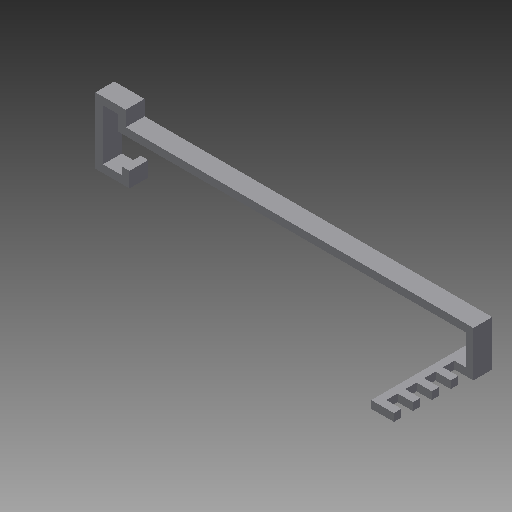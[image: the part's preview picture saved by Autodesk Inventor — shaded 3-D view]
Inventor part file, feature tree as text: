
AUTODESK INVENTOR PART (.ipt)
format: ipt  version: 2018.3 (Build 223284000, 284)  size: 239,616 bytes
history: native  units: mm
features: extrude x19, sketch x19
ambient origin geometry x8: Origin, YZ Plane, XZ Plane, XY Plane, X Axis, Y Axis, Z Axis, Center Point
bodies: Solid1 (feature_tree)
feature tree (38):
  extrude  "Extrusion1"  Depth=2.0mm
  extrude  "Extrusion2"  Depth=2.0mm TaperAngle=0.0deg
  extrude  "Extrusion3"  Depth=4.0mm TaperAngle=0.0deg
  extrude  "Extrusion5"  Depth=89.93mm TaperAngle=0.0deg
  extrude  "Extrusion6"  Depth=2.0mm
  extrude  "Extrusion7"  Depth=5.0mm TaperAngle=0.0deg
  extrude  "Extrusion8"  Depth=5.0mm TaperAngle=0.0deg
  extrude  "Extrusion9"  Depth=2.0mm
  extrude  "Extrusion10"  Depth=2.0mm
  extrude  "Extrusion11"  Depth=2.0mm
  extrude  "Extrusion12"  Depth=2.0mm
  extrude  "Extrusion13"  Depth=5.0mm TaperAngle=0.0deg
  extrude  "Extrusion14"  Depth=4.0mm TaperAngle=0.0deg
  extrude  "Extrusion15"  Depth=10.0mm TaperAngle=0.0deg
  extrude  "Extrusion16"  Depth=4.0mm TaperAngle=0.0deg
  extrude  "Extrusion17"  Depth=2.0mm
  extrude  "Extrusion18"  [1 undecoded]
  extrude  "Extrusion19"  [1 undecoded]
  extrude  "Extrusion20"  [1 undecoded]
  sketch  "Sketch1"  dims[d0=6.0mm d1=2.0mm]
  sketch  "Sketch2"  dims[d2=5.0mm d3=0.0mm d4=2.0mm d5=0.0mm]
  sketch  "Sketch3"  dims[d6=10.5mm d7=0.0mm d11=4.0mm d12=0.0mm]
  sketch  "Sketch5"  dims[d13=2.0mm d14=89.93mm d15=0.0mm]
  sketch  "Sketch6"  dims[d16=2.0mm d17=0.0mm d18=2.0mm]
  sketch  "Sketch7"  dims[d19=10.0mm d20=0.0mm d21=5.0mm d22=0.0mm]
  sketch  "Sketch8"  dims[d23=2.0mm d24=5.0mm d25=0.0mm]
  sketch  "Sketch9"  dims[d26=2.0mm d27=0.0mm d28=2.0mm]
  sketch  "Sketch10"  dims[d29=2.0mm d30=0.0mm d31=2.0mm]
  sketch  "Sketch11"  dims[d32=5.0mm d33=0.0mm d34=2.0mm]
  sketch  "Sketch12"  dims[d35=5.0mm d36=0.0mm d37=2.0mm]
  sketch  "Sketch13"  dims[d38=4.0mm d39=0.0mm d40=5.0mm d41=0.0mm]
  sketch  "Sketch14"  dims[d42=2.0mm d43=4.0mm d44=0.0mm]
  sketch  "Sketch15"  dims[d45=2.0mm d46=10.0mm d47=0.0mm]
  sketch  "Sketch16"  dims[d48=2.0mm d49=4.0mm d50=0.0mm]
  sketch  "Sketch17"  dims[d51=3.0mm d52=2.0mm]
  sketch  "Sketch18"  dims[d53=4.0mm d54=0.0mm]
  sketch  "Sketch19"
  sketch  "Sketch20"
note: 3 required parameter values undecoded (feature->parameter linkage not recoverable at this tier; creation-order binding heuristic only, values carry confidence <= 0.55)
